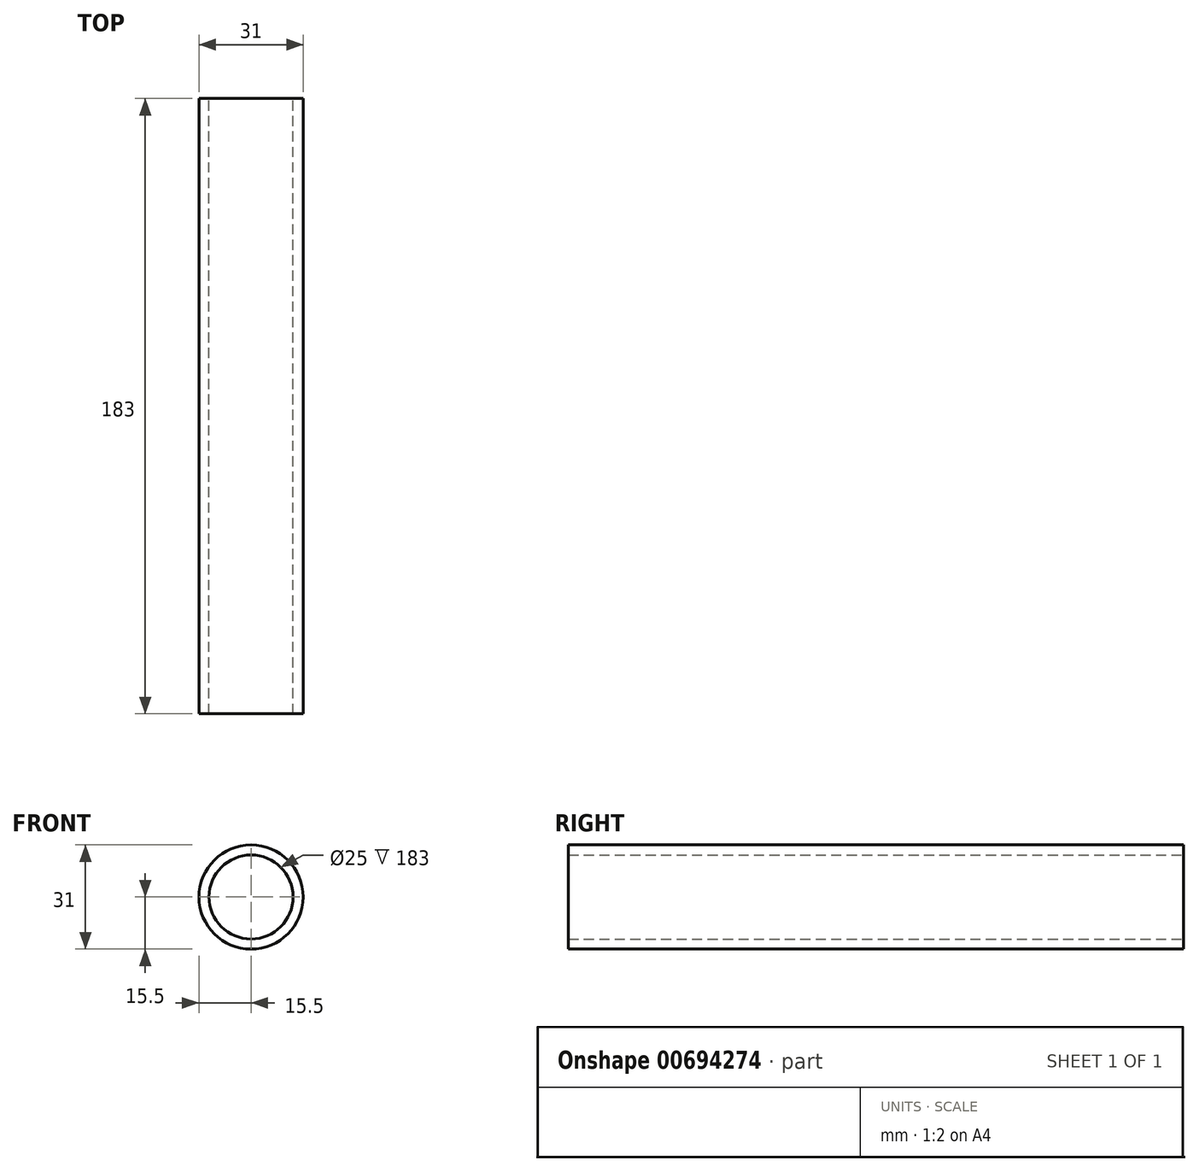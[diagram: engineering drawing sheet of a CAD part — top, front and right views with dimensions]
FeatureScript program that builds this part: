
annotation { "Feature Type Name" : "Feature", "Feature Type Description" : "" }
export const myFeature = defineFeature(function(context is Context, id is Id, definition is map)
    precondition{}
    {
        {
            var Q0;
            Q0=qCreatedBy(makeId("Front.planeOp"),FACE);
            var sketch = newSketch(context, id + "F0", { "sketchPlane" : qUnion([Q0])});
            skCircle(sketch, "E0", {"center": v(0, 0) * mm, "radius": 15.5 * mm});
            skCircle(sketch, "E1", {"center": v(0, 0) * mm, "radius": 12.5 * mm});
            skSolve(sketch);
        }
        {
            var Q0;
            Q0=qSketchRegion(id+"F0",true);
            extrude(context, id + "F1", {"entities" : qUnion([Q0]), "depth" : (150 + 33) * mm, "offsetDistance" : 25 * mm});
        }
    });
